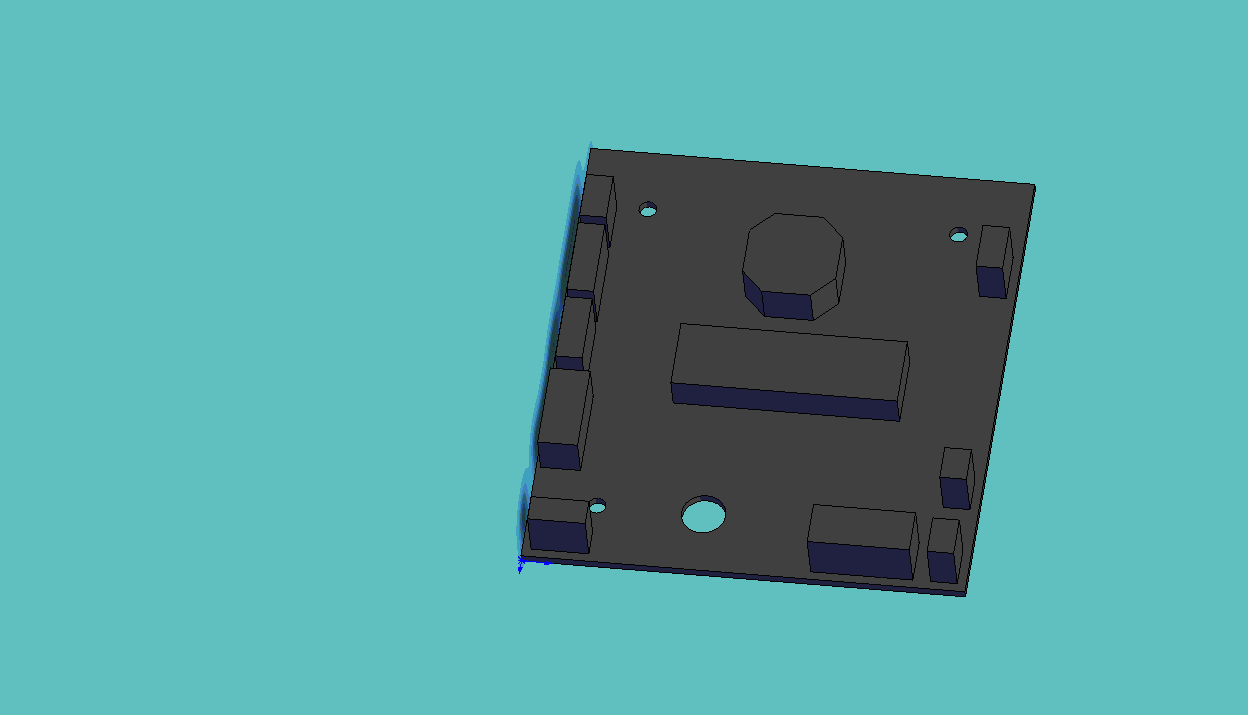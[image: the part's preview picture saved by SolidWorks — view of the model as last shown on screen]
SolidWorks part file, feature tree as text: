
SOLIDWORKS PART (.sldprt)
format: sldprt  version: not decoded by parser v0  size: 314,368 bytes
history: native  units: mm
features: sketch x5, extrude x4, plane x3, material x1, cut_extrude x1, chamfer x1 (+10 scaffold rows collapsed)
feature tree (25):
  scaffold x10  (default folders/planes/origin — collapsed)
  material  "Matériau <non spécifié>"
  plane  "Plan de face"
  plane  "Plan de dessus"
  plane  "Plan de droite"
  sketch  "Esquisse1"  dims[D1=100.0mm D2=110.0mm]
  extrude  "Extrusion1"  Depth=2mm
  sketch  "Esquisse2"  dims[c1.D3=4.0mm c1.D4=10.0mm c1.D5=10.0mm c1.D1=80.0mm c1.D2=70.0mm c2.D5=24.0mm]
  cut_extrude  "Enlèv. mat.-Extru.1"  Depth=10mm
  sketch  "Esquisse3"  dims[c1.D1=2.0mm c1.D2=2.0mm c1.D3=1.0mm c1.D4=2.0mm c1.D5=6.0mm c1.D6=6.0mm c1.D7=2.0mm c1.D8=2.0mm c1.D9=2.0mm c1.D10=23.0mm c1.D11=12.0mm c1.D12=10.0mm c1.D13=13.0mm c1.D14=6.0mm c1.D15=24.0mm c1.D16=20.0mm c1.D17=46.0mm c1.D18=11.0mm c1.D19=18.0mm c1.D20=2.0mm c1.D21=16.0mm c1.D22=2.0mm c1.D23=9.0mm c1.D24=11.0mm c1.D25=22.0mm c1.D26=8.0mm c1.D27=79.0mm c1.D28=9.0mm c1.D29=~39.890639mm c1.D30=16.0mm c1.D31=51.0mm c1.D32=21.0mm c1.D33=21.0mm c1.D34=20.0mm c1.D35=40.0mm c1.D36=28.0mm c2.D29=50.0mm]
  extrude  "Extrusion2"  Depth=12mm
  sketch  "Esquisse4"
  extrude  "Enlèv. mat.-Extru.2"  Depth=2mm
  sketch  "Esquisse5"
  extrude  "Enlèv. mat.-Extru.3"  Depth=4mm
  chamfer  "Chanfrein1"  Distance=5mm Angle=45deg
decode coverage: 9 of 11 modeling features carry decoded parameters
note: ~ marks probable driven/reference dimensions
note: suppression state not decoded; provenance and decode notes live in map.json
